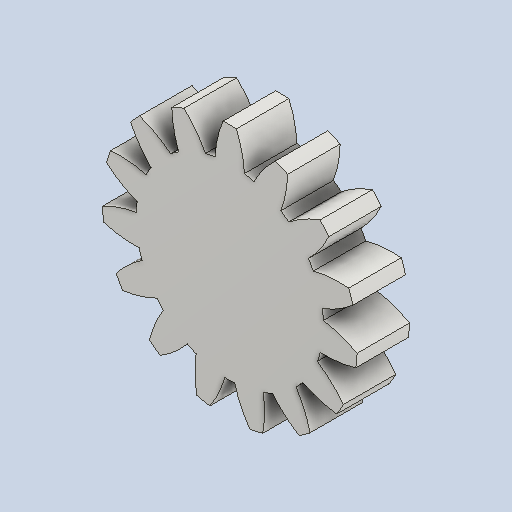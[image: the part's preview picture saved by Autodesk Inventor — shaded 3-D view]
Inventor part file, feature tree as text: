
AUTODESK INVENTOR PART (.ipt)
format: ipt  version: 2025.2 (Build 292293000, 293)  size: 218,624 bytes
history: native  units: mm (DEFAULTED — no unit token found)
features: plane x3, other x3, extrude x1, sketch x1
ambient origin geometry x8: Origin, YZ Plane, XZ Plane, XY Plane, X Axis, Y Axis, Z Axis, Center Point
bodies: Solid1 (feature_tree)
feature tree (8):
  extrude  "Extrusion1"  Depth=7.0mm TaperAngle=0.0deg
  plane  "Work Plane2"
  plane  "Work Plane8"
  plane  "Work Plane9"
  other  "Spur Gear"
  sketch  "Sketch1"  dims[d0=34.0mm d1=7.0mm d2=0.0mm d3=30.0mm d4=10.0mm d5=0.0mm d16=60.0mm d17=0.0mm d34=2.094395mm d39=0.0mm d41=0.0mm d43=60.0mm d46=60.0mm d47=0.0mm d48=0.0mm]
  other  "Srf1"
  other  "Pitch Diameter"
